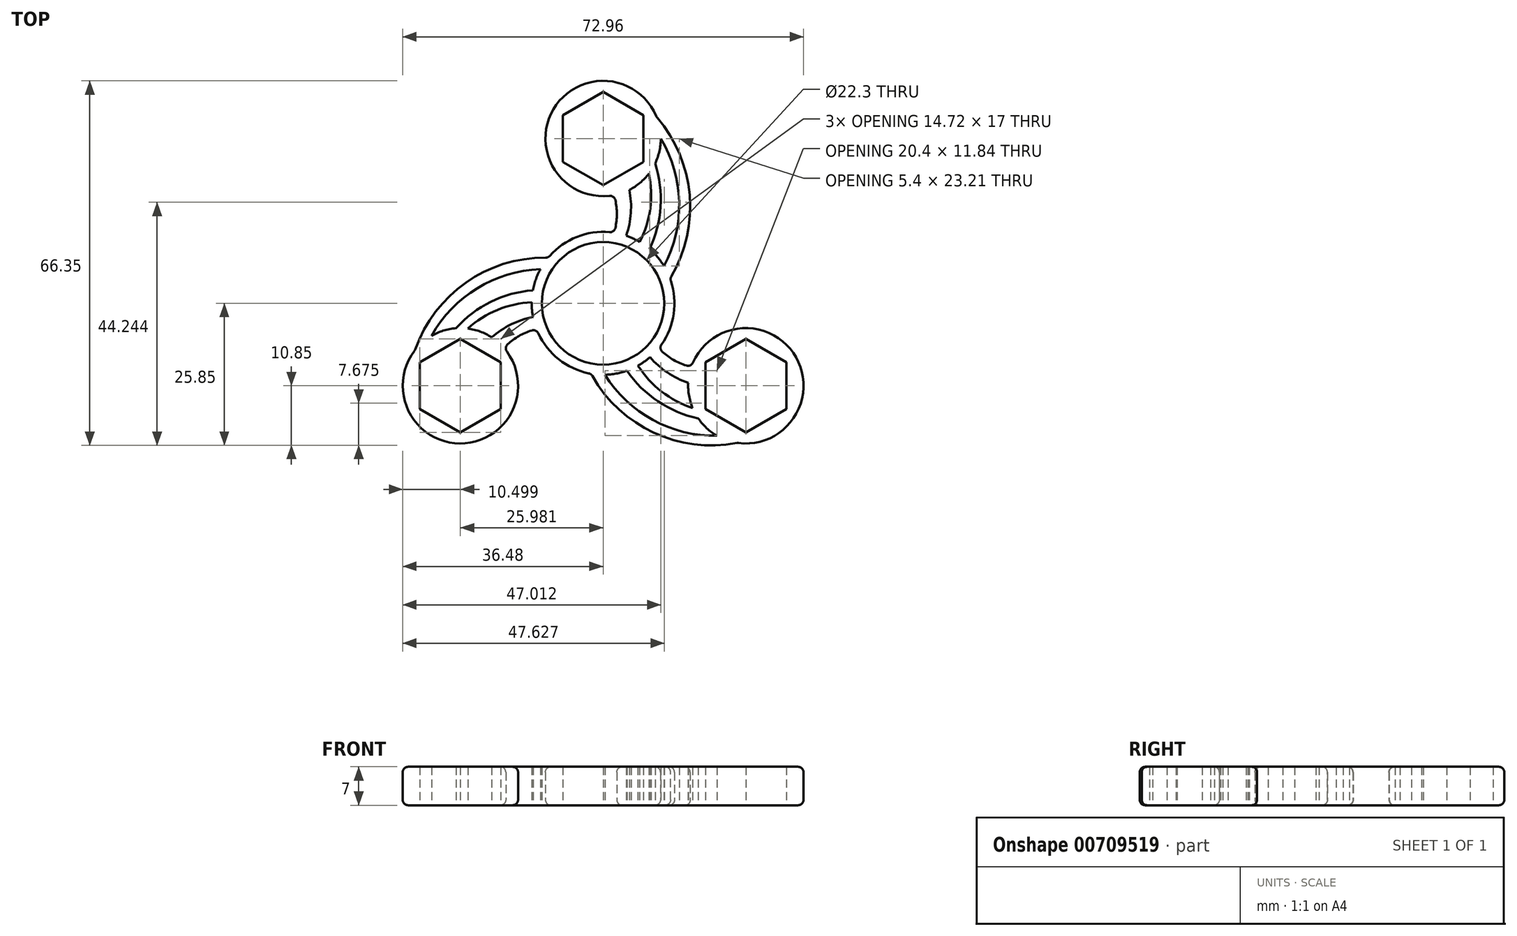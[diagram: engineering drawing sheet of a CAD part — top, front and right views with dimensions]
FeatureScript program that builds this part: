
annotation { "Feature Type Name" : "Feature", "Feature Type Description" : "" }
export const myFeature = defineFeature(function(context is Context, id is Id, definition is map)
    precondition{}
    {
        {
            var Q0;
            Q0=qCreatedBy(makeId("Top.planeOp"),FACE);
            var sketch = newSketch(context, id + "F0", { "sketchPlane" : qUnion([Q0])});
            skCircle(sketch, "E0", {"center": v(0, 0) * mm, "radius": 11.15 * mm});
            skCircle(sketch, "E1", {"center": v(0, 0) * mm, "radius": 13 * mm});
            skCircle(sketch, "E2.cCircle", {"center": v(0, 30) * mm, "radius": 8.5 * mm, "construction": true});
            skLineSegment(sketch, "E2.0", {"start": v(0, 38.5) * mm, "end": v(7.36, 34.25) * mm});
            skLineSegment(sketch, "E2.1", {"start": v(7.36, 34.25) * mm, "end": v(7.36, 25.75) * mm});
            skLineSegment(sketch, "E2.2", {"start": v(7.36, 25.75) * mm, "end": v(0, 21.5) * mm});
            skLineSegment(sketch, "E2.3", {"start": v(0, 21.5) * mm, "end": v(-7.36, 25.75) * mm});
            skLineSegment(sketch, "E2.4", {"start": v(-7.36, 25.75) * mm, "end": v(-7.36, 34.25) * mm});
            skLineSegment(sketch, "E2.5", {"start": v(-7.36, 34.25) * mm, "end": v(0, 38.5) * mm});
            skCircle(sketch, "E3", {"center": v(0, 30) * mm, "radius": 10.5 * mm});
            skArc(sketch, "E4", {"start": v(2, 12.85) * mm, "mid": v(2.5, 16.27) * mm, "end": v(2, 19.7) * mm});
            skArc(sketch, "E5", {"start": v(4.21, 12.3) * mm, "mid": v(5.05, 16.44) * mm, "end": v(4.78, 20.65) * mm});
            skArc(sketch, "E6", {"start": v(6.65, 11.17) * mm, "mid": v(8.58, 17.25) * mm, "end": v(8.34, 23.63) * mm});
            skPoint(sketch, "E6.endSnap0", {"position": v(-3.68, 23.63) * mm});
            skArc(sketch, "E7", {"start": v(8.45, 9.88) * mm, "mid": v(10.46, 17.57) * mm, "end": v(9.47, 25.46) * mm});
            skArc(sketch, "E8", {"start": v(11.09, 6.79) * mm, "mid": v(13.85, 18.47) * mm, "end": v(10.5, 30) * mm});
            skPoint(sketch, "E8.endSnap0", {"position": v(7.36, 30) * mm});
            skArc(sketch, "E9", {"start": v(12.2, 4.52) * mm, "mid": v(15.77, 19.62) * mm, "end": v(9.74, 33.92) * mm});
            skPoint(sketch, "E10.1.0", {"position": v(-18.62, -15) * mm});
            skCircle(sketch, "E10.1.3", {"center": v(-25.98, -15) * mm, "radius": 8.5 * mm, "construction": true});
            skLineSegment(sketch, "E10.1.4", {"start": v(-33.34, -19.25) * mm, "end": v(-33.34, -10.75) * mm});
            skPoint(sketch, "E10.1.5", {"position": v(-29.66, -8.62) * mm});
            skArc(sketch, "E10.1.6", {"start": v(-12.12, -4.7) * mm, "mid": v(-15.34, -5.97) * mm, "end": v(-18.05, -8.11) * mm});
            skLineSegment(sketch, "E10.1.7", {"start": v(-25.98, -6.5) * mm, "end": v(-18.62, -10.75) * mm});
            skArc(sketch, "E10.1.8", {"start": v(-10, 8.3) * mm, "mid": v(-24.87, 3.85) * mm, "end": v(-34.24, -8.52) * mm});
            skArc(sketch, "E10.1.9", {"start": v(-11.42, 6.2) * mm, "mid": v(-22.92, 2.76) * mm, "end": v(-31.23, -5.9) * mm});
            skArc(sketch, "E10.1.10", {"start": v(-12.78, 2.37) * mm, "mid": v(-20.45, 0.28) * mm, "end": v(-26.79, -4.53) * mm});
            skLineSegment(sketch, "E10.1.11", {"start": v(-18.62, -19.25) * mm, "end": v(-25.98, -23.5) * mm});
            skLineSegment(sketch, "E10.1.12", {"start": v(-25.98, -23.5) * mm, "end": v(-33.34, -19.25) * mm});
            skCircle(sketch, "E10.1.13", {"center": v(-25.98, -15) * mm, "radius": 10.5 * mm});
            skArc(sketch, "E10.1.14", {"start": v(-12.76, -2.5) * mm, "mid": v(-16.76, -3.84) * mm, "end": v(-20.27, -6.19) * mm});
            skArc(sketch, "E10.1.15", {"start": v(-13, 0.18) * mm, "mid": v(-19.23, -1.2) * mm, "end": v(-24.63, -4.59) * mm});
            skLineSegment(sketch, "E10.1.16", {"start": v(-33.34, -10.75) * mm, "end": v(-25.98, -6.5) * mm});
            skLineSegment(sketch, "E10.1.17", {"start": v(-18.62, -10.75) * mm, "end": v(-18.62, -19.25) * mm});
            skPoint(sketch, "E10.2.0", {"position": v(22.3, -8.63) * mm});
            skCircle(sketch, "E10.2.3", {"center": v(25.98, -15) * mm, "radius": 8.5 * mm, "construction": true});
            skLineSegment(sketch, "E10.2.4", {"start": v(33.34, -19.25) * mm, "end": v(25.98, -23.5) * mm});
            skPoint(sketch, "E10.2.5", {"position": v(22.3, -21.37) * mm});
            skArc(sketch, "E10.2.6", {"start": v(10.12, -8.15) * mm, "mid": v(12.84, -10.3) * mm, "end": v(16.05, -11.58) * mm});
            skLineSegment(sketch, "E10.2.7", {"start": v(18.62, -19.25) * mm, "end": v(18.62, -10.75) * mm});
            skArc(sketch, "E10.2.8", {"start": v(-2.18, -12.82) * mm, "mid": v(9.1, -23.47) * mm, "end": v(24.5, -25.4) * mm});
            skArc(sketch, "E10.2.9", {"start": v(0.33, -13) * mm, "mid": v(9.07, -21.23) * mm, "end": v(20.73, -24.1) * mm});
            skArc(sketch, "E10.2.10", {"start": v(4.34, -12.26) * mm, "mid": v(9.99, -17.85) * mm, "end": v(17.32, -20.93) * mm});
            skLineSegment(sketch, "E10.2.11", {"start": v(25.98, -6.5) * mm, "end": v(33.34, -10.75) * mm});
            skLineSegment(sketch, "E10.2.12", {"start": v(33.34, -10.75) * mm, "end": v(33.34, -19.25) * mm});
            skCircle(sketch, "E10.2.13", {"center": v(25.98, -15) * mm, "radius": 10.5 * mm});
            skArc(sketch, "E10.2.14", {"start": v(8.55, -9.8) * mm, "mid": v(11.7, -12.6) * mm, "end": v(15.5, -14.46) * mm});
            skArc(sketch, "E10.2.15", {"start": v(6.35, -11.35) * mm, "mid": v(10.65, -16.05) * mm, "end": v(16.29, -19.04) * mm});
            skLineSegment(sketch, "E10.2.16", {"start": v(25.98, -23.5) * mm, "end": v(18.62, -19.25) * mm});
            skLineSegment(sketch, "E10.2.17", {"start": v(18.62, -10.75) * mm, "end": v(25.98, -6.5) * mm});
            skSolve(sketch);
        }
        {
            var Q0;
            {var subQ0=sQuery(id+"F0.wireOp",EDGE,"E10.1.8");Q0=makeQuery(id+"F0.imprint","IMPRINT",FACE,{"disambiguationData":[TD([[makeQuery(id+"F0.imprint","IMPRINT",EDGE,{"derivedFrom":subQ0}),1.0]])]});}
            var Q1;
            {var subQ0=sQuery(id+"F0.wireOp",EDGE,"E10.1.10");Q1=makeQuery(id+"F0.imprint","IMPRINT",FACE,{"disambiguationData":[TD([[makeQuery(id+"F0.imprint","IMPRINT",EDGE,{"derivedFrom":subQ0}),1.0]])]});}
            var Q2;
            {var subQ0=sQuery(id+"F0.wireOp",EDGE,"E10.1.6");Q2=makeQuery(id+"F0.imprint","IMPRINT",FACE,{"disambiguationData":[TD([[makeQuery(id+"F0.imprint","IMPRINT",EDGE,{"derivedFrom":subQ0}),-1.0]])]});}
            var Q3;
            Q3=makeQuery(id+"F0.imprint","IMPRINT",FACE,{"disambiguationData":[TD([[makeQuery(id+"F0.imprint","IMPRINT",EDGE,{"derivedFrom":sQuery(id+"F0.wireOp",EDGE,"E10.1.4")}),1.0]])]});
            var Q4;
            Q4=makeQuery(id+"F0.imprint","IMPRINT",FACE,{"disambiguationData":[TD([[makeQuery(id+"F0.imprint","IMPRINT",EDGE,{"derivedFrom":sQuery(id+"F0.wireOp",EDGE,"E0")}),-1.0]])]});
            var Q5;
            {var subQ0=sQuery(id+"F0.wireOp",EDGE,"E10.2.8");Q5=makeQuery(id+"F0.imprint","IMPRINT",FACE,{"disambiguationData":[TD([[makeQuery(id+"F0.imprint","IMPRINT",EDGE,{"derivedFrom":subQ0}),1.0]])]});}
            var Q6;
            {var subQ0=sQuery(id+"F0.wireOp",EDGE,"E10.2.10");Q6=makeQuery(id+"F0.imprint","IMPRINT",FACE,{"disambiguationData":[TD([[makeQuery(id+"F0.imprint","IMPRINT",EDGE,{"derivedFrom":subQ0}),1.0]])]});}
            var Q7;
            {var subQ0=sQuery(id+"F0.wireOp",EDGE,"E10.2.6");Q7=makeQuery(id+"F0.imprint","IMPRINT",FACE,{"disambiguationData":[TD([[makeQuery(id+"F0.imprint","IMPRINT",EDGE,{"derivedFrom":subQ0}),-1.0]])]});}
            var Q8;
            Q8=makeQuery(id+"F0.imprint","IMPRINT",FACE,{"disambiguationData":[TD([[makeQuery(id+"F0.imprint","IMPRINT",EDGE,{"derivedFrom":sQuery(id+"F0.wireOp",EDGE,"E10.2.4")}),1.0]])]});
            var Q9;
            {var subQ0=sQuery(id+"F0.wireOp",EDGE,"E8");Q9=makeQuery(id+"F0.imprint","IMPRINT",FACE,{"disambiguationData":[TD([[makeQuery(id+"F0.imprint","IMPRINT",EDGE,{"derivedFrom":subQ0}),-1.0]])]});}
            var Q10;
            {var subQ0=sQuery(id+"F0.wireOp",EDGE,"E6");Q10=makeQuery(id+"F0.imprint","IMPRINT",FACE,{"disambiguationData":[TD([[makeQuery(id+"F0.imprint","IMPRINT",EDGE,{"derivedFrom":subQ0}),-1.0]])]});}
            var Q11;
            {var subQ0=sQuery(id+"F0.wireOp",EDGE,"E4");Q11=makeQuery(id+"F0.imprint","IMPRINT",FACE,{"disambiguationData":[TD([[makeQuery(id+"F0.imprint","IMPRINT",EDGE,{"derivedFrom":subQ0}),-1.0]])]});}
            var Q12;
            Q12=makeQuery(id+"F0.imprint","IMPRINT",FACE,{"disambiguationData":[TD([[makeQuery(id+"F0.imprint","IMPRINT",EDGE,{"derivedFrom":sQuery(id+"F0.wireOp",EDGE,"E2.0")}),1.0]])]});
            extrude(context, id + "F1", {"entities" : qUnion([Q0, Q1, Q2, Q3, Q4, Q5, Q6, Q7, Q8, Q9, Q10, Q11, Q12]), "depth" : 7 * mm, "offsetDistance" : 25 * mm});
        }
        {
            var Q0;
            {var subQ0=sQuery(id+"F0.wireOp",EDGE,"E10.1.13");Q0=makeQuery(id+"F1.opExtrude","SWEPT_FACE",FACE,{"disambiguationData":[OSD([subQ0]),TDD([makeQuery(id+"F0.imprint","IMPRINT",EDGE,{"disambiguationData":[TD([[makeQuery(id+"F0.imprint","INTERSECT",VERTEX,{"derivedFrom":[sQuery(id+"F0.wireOp",EDGE,"E10.1.6"),subQ0]}),1.0]])],"derivedFrom":subQ0})])]});}
            var Q1;
            {var subQ0=sQuery(id+"F0.wireOp",EDGE,"E1");Q1=makeQuery(id+"F1.opExtrude","SWEPT_FACE",FACE,{"disambiguationData":[OSD([subQ0]),TDD([makeQuery(id+"F0.imprint","IMPRINT",EDGE,{"disambiguationData":[TD([[makeQuery(id+"F0.imprint","INTERSECT",VERTEX,{"derivedFrom":[sQuery(id+"F0.wireOp",EDGE,"E10.1.6"),subQ0]}),-1.0]])],"derivedFrom":subQ0})])]});}
            var Q2;
            Q2=makeQuery(id+"F1.opExtrude","SWEPT_FACE",FACE,{"disambiguationData":[OSD([sQuery(id+"F0.wireOp",EDGE,"E10.1.6")])]});
            var Q3;
            Q3=makeQuery(id+"F1.opExtrude","SWEPT_FACE",FACE,{"disambiguationData":[OSD([sQuery(id+"F0.wireOp",EDGE,"E10.2.8")])]});
            var Q4;
            {var subQ0=sQuery(id+"F0.wireOp",EDGE,"E10.2.13");Q4=makeQuery(id+"F1.opExtrude","SWEPT_FACE",FACE,{"disambiguationData":[OSD([subQ0]),TDD([makeQuery(id+"F0.imprint","IMPRINT",EDGE,{"disambiguationData":[TD([[makeQuery(id+"F0.imprint","INTERSECT",VERTEX,{"derivedFrom":[sQuery(id+"F0.wireOp",EDGE,"E10.2.6"),subQ0]}),1.0]])],"derivedFrom":subQ0})])]});}
            var Q5;
            Q5=makeQuery(id+"F1.opExtrude","SWEPT_FACE",FACE,{"disambiguationData":[OSD([sQuery(id+"F0.wireOp",EDGE,"E10.2.6")])]});
            var Q6;
            {var subQ0=sQuery(id+"F0.wireOp",EDGE,"E1");Q6=makeQuery(id+"F1.opExtrude","SWEPT_FACE",FACE,{"disambiguationData":[OSD([subQ0]),TDD([makeQuery(id+"F0.imprint","IMPRINT",EDGE,{"disambiguationData":[TD([[makeQuery(id+"F0.imprint","INTERSECT",VERTEX,{"derivedFrom":[sQuery(id+"F0.wireOp",EDGE,"E9"),subQ0]}),1.0]])],"derivedFrom":subQ0})])]});}
            var Q7;
            Q7=makeQuery(id+"F1.opExtrude","SWEPT_FACE",FACE,{"disambiguationData":[OSD([sQuery(id+"F0.wireOp",EDGE,"E9")])]});
            var Q8;
            {var subQ0=sQuery(id+"F0.wireOp",EDGE,"E3");Q8=makeQuery(id+"F1.opExtrude","SWEPT_FACE",FACE,{"disambiguationData":[OSD([subQ0]),TDD([makeQuery(id+"F0.imprint","IMPRINT",EDGE,{"disambiguationData":[TD([[makeQuery(id+"F0.imprint","INTERSECT",VERTEX,{"derivedFrom":[subQ0,sQuery(id+"F0.wireOp",EDGE,"E4")]}),1.0]])],"derivedFrom":subQ0})])]});}
            var Q9;
            Q9=makeQuery(id+"F1.opExtrude","SWEPT_FACE",FACE,{"disambiguationData":[OSD([sQuery(id+"F0.wireOp",EDGE,"E4")])]});
            var Q10;
            {var subQ0=sQuery(id+"F0.wireOp",EDGE,"E1");Q10=makeQuery(id+"F1.opExtrude","SWEPT_FACE",FACE,{"disambiguationData":[OSD([subQ0]),TDD([makeQuery(id+"F0.imprint","IMPRINT",EDGE,{"disambiguationData":[TD([[makeQuery(id+"F0.imprint","INTERSECT",VERTEX,{"derivedFrom":[sQuery(id+"F0.wireOp",EDGE,"E4"),subQ0]}),-1.0]])],"derivedFrom":subQ0})])]});}
            var Q11;
            Q11=makeQuery(id+"F1.opExtrude","SWEPT_FACE",FACE,{"disambiguationData":[OSD([sQuery(id+"F0.wireOp",EDGE,"E10.1.8")])]});
            fillet(context, id + "F2", {"entities" : qUnion([Q0, Q1, Q2, Q3, Q4, Q5, Q6, Q7, Q8, Q9, Q10, Q11]), "radius" : 1 * mm, "tangentPropagation" : true, "allowEdgeOverflow" : false});
        }
    });
